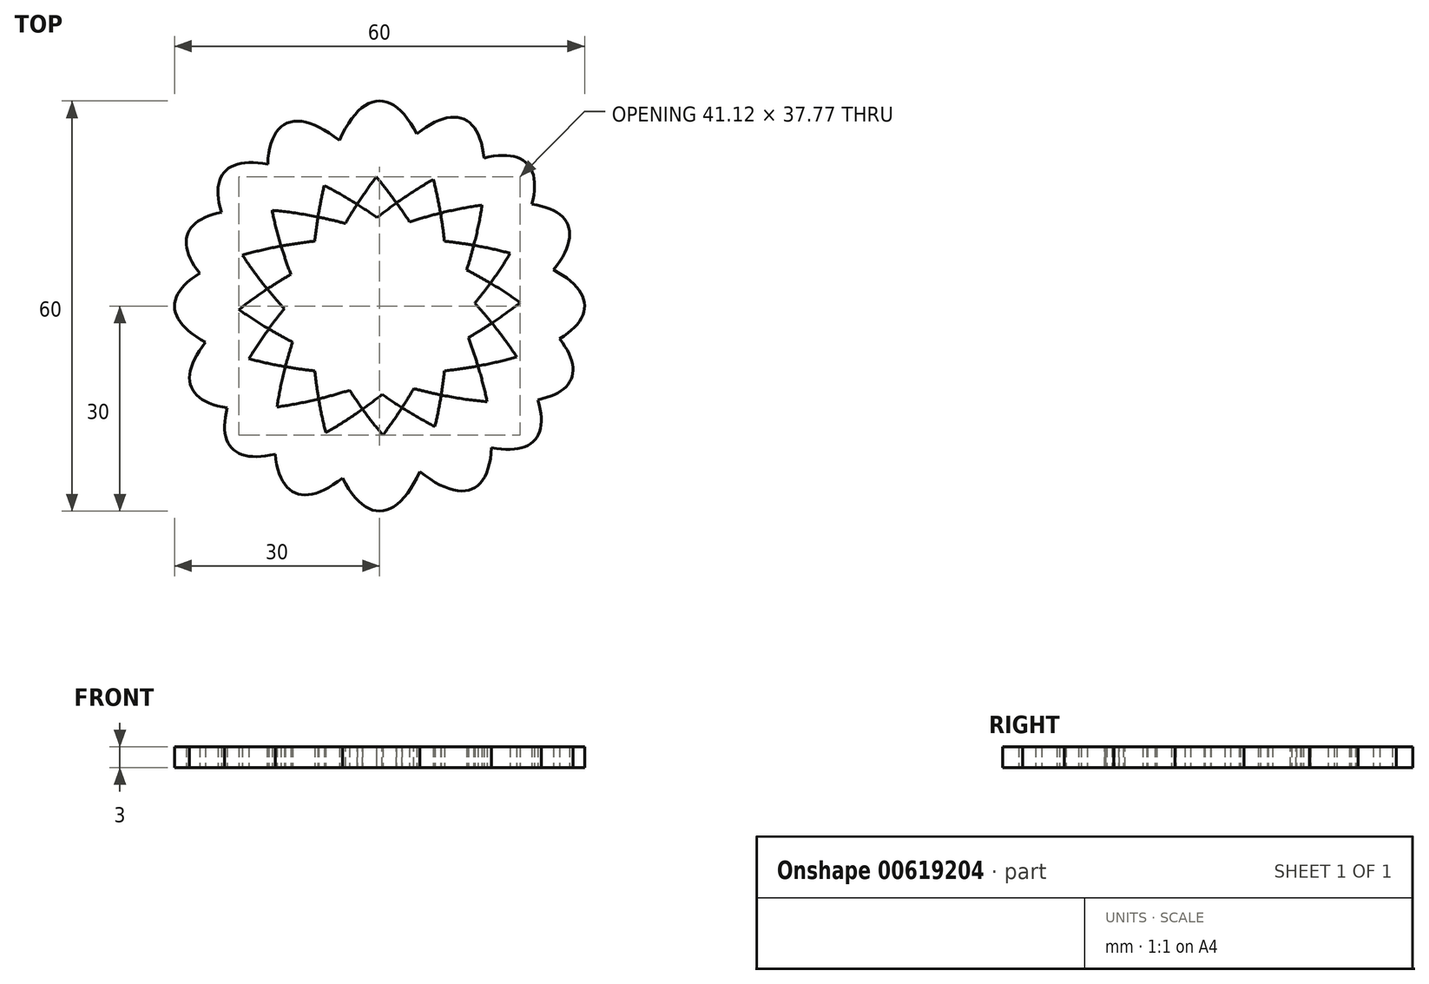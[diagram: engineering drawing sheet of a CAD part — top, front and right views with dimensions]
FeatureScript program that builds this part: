
annotation { "Feature Type Name" : "Feature", "Feature Type Description" : "" }
export const myFeature = defineFeature(function(context is Context, id is Id, definition is map)
    precondition{}
    {
        {
            var Q0;
            Q0=qCreatedBy(makeId("Top.planeOp"),FACE);
            var sketch = newSketch(context, id + "F0", { "sketchPlane" : qUnion([Q0])});
            skEllipticalArc(sketch, "E0", {});
            skEllipticalArc(sketch, "E1", {});
            skEllipticalArc(sketch, "E2", {});
            skEllipticalArc(sketch, "E3", {});
            skEllipticalArc(sketch, "E4", {});
            skEllipticalArc(sketch, "E5", {});
            skEllipticalArc(sketch, "E6", {});
            skEllipticalArc(sketch, "E7", {});
            skEllipticalArc(sketch, "E8.trimOffspring", {});
            skEllipticalArc(sketch, "E9.trimOffspring", {});
            skEllipticalArc(sketch, "E10.trimOffspring", {});
            skEllipticalArc(sketch, "E11.trimOffspring", {});
            skEllipticalArc(sketch, "E12.trimOffspring", {});
            skEllipticalArc(sketch, "E13.trimOffspring", {});
            skEllipticalArc(sketch, "E14.trimOffspring", {});
            skEllipticalArc(sketch, "E15.trimOffspring", {});
            skEllipticalArc(sketch, "E16.trimOffspring", {});
            skEllipticalArc(sketch, "E17.trimOffspring", {});
            skEllipticalArc(sketch, "E18.trimOffspring", {});
            skEllipticalArc(sketch, "E19.trimOffspring", {});
            skEllipticalArc(sketch, "E20.trimOffspring", {});
            skEllipticalArc(sketch, "E21.trimOffspring", {});
            skEllipticalArc(sketch, "E22.trimOffspring", {});
            skEllipticalArc(sketch, "E23.trimOffspring", {});
            skEllipticalArc(sketch, "E24.trimOffspring", {});
            skEllipticalArc(sketch, "E25.trimOffspring", {});
            skEllipticalArc(sketch, "E26.trimOffspring", {});
            skEllipticalArc(sketch, "E27.trimOffspring", {});
            skEllipticalArc(sketch, "E28.trimOffspring", {});
            skEllipticalArc(sketch, "E29.trimOffspring", {});
            skEllipticalArc(sketch, "E30.trimOffspring", {});
            skEllipticalArc(sketch, "E31.trimOffspring", {});
            skEllipticalArc(sketch, "E32", {});
            skEllipticalArc(sketch, "E33", {});
            skEllipticalArc(sketch, "E34", {});
            skEllipticalArc(sketch, "E35", {});
            skEllipticalArc(sketch, "E36", {});
            skEllipticalArc(sketch, "E37", {});
            skEllipticalArc(sketch, "E38", {});
            skEllipticalArc(sketch, "E39", {});
            skEllipticalArc(sketch, "E40", {});
            skEllipticalArc(sketch, "E41", {});
            skEllipticalArc(sketch, "E42", {});
            skEllipticalArc(sketch, "E43", {});
            skEllipticalArc(sketch, "E44", {});
            skEllipticalArc(sketch, "E45", {});
            skEllipticalArc(sketch, "E46", {});
            skEllipticalArc(sketch, "E47", {});
            const initialGuessF0  = {"E0": [0, 0, 0, -1, 0.03, 0.01, 5.707652658227705, 0], "E1": [0, 0, -1, 0, 0.03, 0.01, 2.642024951638131, 3.141592653589793], "E2": [0, 0, 0.719676517800556, 0.6943095201179845, 0.03, 0.01, 4.047013061400929, 5.402548984350965], "E3": [0, 0, -0.7581335094198967, 0.6520993650469777, 0.03, 0.01, 2.6137857632382424, 3.141592653589793], "E4": [0, 0, -0.45874326626276485, 0.8885688581413205, 0.03, 0.01, 2.511853225270534, 3.141592653589793], "E5": [0, 0, 0.41320832804158036, 0.9106365233379791, 0.03, 0.01, 4.109892639118385, 5.42593323517256], "E6": [0, 0, -0.9359348451973232, 0.35217320390038603, 0.03, 0.01, 2.653348630316495, 3.141592653589793], "E7": [0, 0, -0.9172268162763845, -0.3983653693576886, 0.03, 0.01, 2.584183450086654, 3.141592653589793], "E8.trimOffspring": [0, 0, 0, -1, 0.03, 0.01, 0.9425783349267141, 2.2361722457786577], "E9.trimOffspring": [0, 0, -0.45874326626276485, 0.8885688581413205, 0.03, 0.01, 3.998280747334294, 5.314885321650993], "E10.trimOffspring": [0, 0, -0.7581335094198967, 0.6520993650469777, 0.03, 0.01, 3.9802901965482214, 5.340606972252871], "E11.trimOffspring": [0, 0, -0.9359348451973232, 0.35217320390038603, 0.03, 0.01, 4.023758446463335, 5.426497213435084], "E12.trimOffspring": [0, 0, -1, 0, 0.03, 0.01, 4.022228976418415, 5.444487764221157], "E13.trimOffspring": [0, 0, 0.719676517800556, 0.6943095201179845, 0.03, 0.01, 5.78620703741481, 0], "E14.trimOffspring": [0, 0, -0.9172268162763845, -0.3983653693576886, 0.03, 0.01, 3.9988447255968187, 5.401019514306045], "E15.trimOffspring": [0, 0, 0.41320832804158036, 0.9106365233379791, 0.03, 0.01, 5.7629630431196155, 0], "E16.trimOffspring": [0, 0, 0.719676517800556, 0.6943095201179845, 0.03, 0.01, 0.9054204078111355, 2.260956330761171], "E17.trimOffspring": [0, 0, 0, -1, 0.03, 0.01, 2.566060004637914, 3.141592653589793], "E18.trimOffspring": [0, 0, 0.41320832804158036, 0.9106365233379791, 0.03, 0.01, 0.9682999855285929, 2.284340581582767], "E19.trimOffspring": [0, 0, -0.45874326626276485, 0.8885688581413205, 0.03, 0.01, 5.653445878860328, 0], "E20.trimOffspring": [0, 0, 0, -1, 0.03, 0.01, 4.084170988516508, 5.377764899368451], "E21.trimOffspring": [0, 0, -0.7581335094198967, 0.6520993650469777, 0.03, 0.01, 5.7553784168280355, 0], "E22.trimOffspring": [0, 0, -0.45874326626276485, 0.8885688581413205, 0.03, 0.01, 0.856688093744502, 2.1732926680612006], "E23.trimOffspring": [0, 0, -0.9359348451973232, 0.35217320390038603, 0.03, 0.01, 5.7949412839062875, 0], "E24.trimOffspring": [0, 0, -0.7581335094198967, 0.6520993650469777, 0.03, 0.01, 0.8386975429584291, 2.199014318663079], "E25.trimOffspring": [0, 0, -1, 0, 0.03, 0.01, 5.783617605227924, 0], "E26.trimOffspring": [0, 0, -0.9359348451973232, 0.35217320390038603, 0.03, 0.01, 0.8821657928735414, 2.284904559845293], "E27.trimOffspring": [0, 0, -0.9172268162763845, -0.3983653693576886, 0.03, 0.01, 5.725776103676448, 0], "E28.trimOffspring": [0, 0, -1, 0, 0.03, 0.01, 0.8806363228286226, 2.3028951106313644], "E29.trimOffspring": [0, 0, 0.719676517800556, 0.6943095201179845, 0.03, 0.01, 2.644614383825017, 3.141592653589793], "E30.trimOffspring": [0, 0, -0.9172268162763845, -0.3983653693576886, 0.03, 0.01, 0.857252072007026, 2.2594268607162515], "E31.trimOffspring": [0, 0, 0.41320832804158036, 0.9106365233379791, 0.03, 0.01, 2.6213703895298224, 3.141592653589793], "E32": [0, 0, -1, 0, 0.03, 0.01, 0, 0.5574092035031396], "E33": [0, 0, -0.9172268162763845, -0.3983653693576886, 0.03, 0.01, 0, 0.4969782697647762], "E34": [0, 0, 0.719676517800556, 0.6943095201179845, 0.03, 0.01, 3.141592653589793, 3.6618149176497643], "E35": [0, 0, 0.41320832804158036, 0.9106365233379791, 0.03, 0.01, 3.141592653589793, 3.7171253025416737], "E36": [0, 0, 0, -1, 0.03, 0.01, 0, 0.6297394283192591], "E37": [0, 0, -0.45874326626276485, 0.8885688581413205, 0.03, 0.01, 3.141592653589793, 3.6693995439413434], "E38": [0, 0, -0.7581335094198967, 0.6520993650469777, 0.03, 0.01, 3.141592653589793, 3.6298366768630923], "E39": [0, 0, -0.9359348451973232, 0.35217320390038603, 0.03, 0.01, 3.141592653589793, 3.6411603555414533], "E40": [0, 0, -1, 0, 0.03, 0.01, 3.141592653589793, 3.6990018570929326], "E41": [0, 0, -0.9172268162763845, -0.3983653693576886, 0.03, 0.01, 3.141592653589793, 3.6385709233545684], "E42": [0, 0, 0.719676517800556, 0.6943095201179845, 0.03, 0.01, 0, 0.5202222640599707], "E43": [0, 0, 0.41320832804158036, 0.9106365233379791, 0.03, 0.01, 0, 0.5755326489518812], "E44": [0, 0, 0, -1, 0.03, 0.01, 3.141592653589793, 3.7713320819090503], "E45": [0, 0, -0.45874326626276485, 0.8885688581413205, 0.03, 0.01, 0, 0.5278068903515505], "E46": [0, 0, -0.7581335094198967, 0.6520993650469777, 0.03, 0.01, 0, 0.48824402327329985], "E47": [0, 0, -0.9359348451973232, 0.35217320390038603, 0.03, 0.01, 0, 0.4995677019516617]};
            skSetInitialGuess(sketch, initialGuessF0);
            skSolve(sketch);
        }
        {
            var Q0;
            Q0=makeQuery(id+"F0.imprint","IMPRINT",FACE,{"disambiguationData":[TD([[makeQuery(id+"F0.imprint","IMPRINT",EDGE,{"derivedFrom":sQuery(id+"F0.wireOp",EDGE,"E0")}),1.0]])]});
            var Q1;
            {var subQ17=sQuery(id+"F0.wireOp",EDGE,"E2");var subQ21=sQuery(id+"F0.wireOp",EDGE,"E30.trimOffspring");var subQ22=makeQuery(id+"F0.imprint","INTERSECT",VERTEX,{"derivedFrom":[subQ17,subQ21]});Q1=makeQuery(id+"F0.imprint","IMPRINT",FACE,{"disambiguationData":[TD([[makeQuery(id+"F0.imprint","IMPRINT",EDGE,{"disambiguationData":[TD([[subQ22,-1.0]])],"derivedFrom":subQ17}),1.0]])]});}
            var Q2;
            {var subQ0=sQuery(id+"F0.wireOp",EDGE,"E14.trimOffspring");var subQ1=sQuery(id+"F0.wireOp",EDGE,"E9.trimOffspring");var subQ2=makeQuery(id+"F0.imprint","INTERSECT",VERTEX,{"derivedFrom":[subQ1,subQ0]});Q2=makeQuery(id+"F0.imprint","IMPRINT",FACE,{"disambiguationData":[TD([[makeQuery(id+"F0.imprint","IMPRINT",EDGE,{"disambiguationData":[TD([[subQ2,-1.0]])],"derivedFrom":subQ1}),1.0]])]});}
            var Q3;
            {var subQ0=sQuery(id+"F0.wireOp",EDGE,"E12.trimOffspring");var subQ1=sQuery(id+"F0.wireOp",EDGE,"E8.trimOffspring");var subQ2=makeQuery(id+"F0.imprint","INTERSECT",VERTEX,{"derivedFrom":[subQ1,subQ0]});Q3=makeQuery(id+"F0.imprint","IMPRINT",FACE,{"disambiguationData":[TD([[makeQuery(id+"F0.imprint","IMPRINT",EDGE,{"disambiguationData":[TD([[subQ2,-1.0]])],"derivedFrom":subQ1}),1.0]])]});}
            var Q4;
            {var subQ0=sQuery(id+"F0.wireOp",EDGE,"E11.trimOffspring");var subQ1=sQuery(id+"F0.wireOp",EDGE,"E8.trimOffspring");var subQ2=makeQuery(id+"F0.imprint","INTERSECT",VERTEX,{"derivedFrom":[subQ1,subQ0]});Q4=makeQuery(id+"F0.imprint","IMPRINT",FACE,{"disambiguationData":[TD([[makeQuery(id+"F0.imprint","IMPRINT",EDGE,{"disambiguationData":[TD([[subQ2,-1.0]])],"derivedFrom":subQ1}),1.0]])]});}
            var Q5;
            {var subQ0=sQuery(id+"F0.wireOp",EDGE,"E11.trimOffspring");var subQ1=sQuery(id+"F0.wireOp",EDGE,"E5");var subQ2=makeQuery(id+"F0.imprint","INTERSECT",VERTEX,{"derivedFrom":[subQ1,subQ0]});Q5=makeQuery(id+"F0.imprint","IMPRINT",FACE,{"disambiguationData":[TD([[makeQuery(id+"F0.imprint","IMPRINT",EDGE,{"disambiguationData":[TD([[subQ2,-1.0]])],"derivedFrom":subQ1}),1.0]])]});}
            var Q6;
            {var subQ0=sQuery(id+"F0.wireOp",EDGE,"E10.trimOffspring");var subQ1=sQuery(id+"F0.wireOp",EDGE,"E5");var subQ2=makeQuery(id+"F0.imprint","INTERSECT",VERTEX,{"derivedFrom":[subQ1,subQ0]});Q6=makeQuery(id+"F0.imprint","IMPRINT",FACE,{"disambiguationData":[TD([[makeQuery(id+"F0.imprint","IMPRINT",EDGE,{"disambiguationData":[TD([[subQ2,-1.0]])],"derivedFrom":subQ1}),1.0]])]});}
            var Q7;
            {var subQ0=sQuery(id+"F0.wireOp",EDGE,"E10.trimOffspring");var subQ1=sQuery(id+"F0.wireOp",EDGE,"E2");var subQ2=makeQuery(id+"F0.imprint","INTERSECT",VERTEX,{"derivedFrom":[subQ1,subQ0]});Q7=makeQuery(id+"F0.imprint","IMPRINT",FACE,{"disambiguationData":[TD([[makeQuery(id+"F0.imprint","IMPRINT",EDGE,{"disambiguationData":[TD([[subQ2,-1.0]])],"derivedFrom":subQ1}),1.0]])]});}
            var Q8;
            {var subQ0=sQuery(id+"F0.wireOp",EDGE,"E10.trimOffspring");var subQ1=sQuery(id+"F0.wireOp",EDGE,"E8.trimOffspring");var subQ2=makeQuery(id+"F0.imprint","INTERSECT",VERTEX,{"derivedFrom":[subQ1,subQ0]});Q8=makeQuery(id+"F0.imprint","IMPRINT",FACE,{"disambiguationData":[TD([[makeQuery(id+"F0.imprint","IMPRINT",EDGE,{"disambiguationData":[TD([[subQ2,-1.0]])],"derivedFrom":subQ1}),1.0]])]});}
            var Q9;
            {var subQ0=sQuery(id+"F0.wireOp",EDGE,"E9.trimOffspring");var subQ1=sQuery(id+"F0.wireOp",EDGE,"E2");var subQ2=makeQuery(id+"F0.imprint","INTERSECT",VERTEX,{"derivedFrom":[subQ1,subQ0]});Q9=makeQuery(id+"F0.imprint","IMPRINT",FACE,{"disambiguationData":[TD([[makeQuery(id+"F0.imprint","IMPRINT",EDGE,{"disambiguationData":[TD([[subQ2,-1.0]])],"derivedFrom":subQ1}),1.0]])]});}
            var Q10;
            {var subQ0=sQuery(id+"F0.wireOp",EDGE,"E9.trimOffspring");var subQ1=sQuery(id+"F0.wireOp",EDGE,"E2");var subQ2=makeQuery(id+"F0.imprint","INTERSECT",VERTEX,{"derivedFrom":[subQ1,subQ0]});Q10=makeQuery(id+"F0.imprint","IMPRINT",FACE,{"disambiguationData":[TD([[makeQuery(id+"F0.imprint","IMPRINT",EDGE,{"disambiguationData":[TD([[subQ2,-1.0]])],"derivedFrom":subQ1}),-1.0]])]});}
            var Q11;
            {var subQ0=sQuery(id+"F0.wireOp",EDGE,"E28.trimOffspring");var subQ1=sQuery(id+"F0.wireOp",EDGE,"E8.trimOffspring");var subQ2=makeQuery(id+"F0.imprint","INTERSECT",VERTEX,{"derivedFrom":[subQ1,subQ0]});Q11=makeQuery(id+"F0.imprint","IMPRINT",FACE,{"disambiguationData":[TD([[makeQuery(id+"F0.imprint","IMPRINT",EDGE,{"disambiguationData":[TD([[subQ2,-1.0]])],"derivedFrom":subQ1}),-1.0]])]});}
            var Q12;
            {var subQ0=sQuery(id+"F0.wireOp",EDGE,"E8.trimOffspring");var subQ1=sQuery(id+"F0.wireOp",EDGE,"E2");var subQ2=makeQuery(id+"F0.imprint","INTERSECT",VERTEX,{"derivedFrom":[subQ1,subQ0]});Q12=makeQuery(id+"F0.imprint","IMPRINT",FACE,{"disambiguationData":[TD([[makeQuery(id+"F0.imprint","IMPRINT",EDGE,{"disambiguationData":[TD([[subQ2,-1.0]])],"derivedFrom":subQ1}),1.0]])]});}
            var Q13;
            {var subQ0=sQuery(id+"F0.wireOp",EDGE,"E8.trimOffspring");var subQ1=sQuery(id+"F0.wireOp",EDGE,"E2");var subQ2=makeQuery(id+"F0.imprint","INTERSECT",VERTEX,{"derivedFrom":[subQ1,subQ0]});Q13=makeQuery(id+"F0.imprint","IMPRINT",FACE,{"disambiguationData":[TD([[makeQuery(id+"F0.imprint","IMPRINT",EDGE,{"disambiguationData":[TD([[subQ2,-1.0]])],"derivedFrom":subQ1}),-1.0]])]});}
            var Q14;
            {var subQ0=sQuery(id+"F0.wireOp",EDGE,"E5");var subQ1=sQuery(id+"F0.wireOp",EDGE,"E2");var subQ2=makeQuery(id+"F0.imprint","INTERSECT",VERTEX,{"derivedFrom":[subQ1,subQ0]});Q14=makeQuery(id+"F0.imprint","IMPRINT",FACE,{"disambiguationData":[TD([[makeQuery(id+"F0.imprint","IMPRINT",EDGE,{"disambiguationData":[TD([[subQ2,-1.0]])],"derivedFrom":subQ1}),-1.0]])]});}
            var Q15;
            {var subQ0=sQuery(id+"F0.wireOp",EDGE,"E28.trimOffspring");var subQ1=sQuery(id+"F0.wireOp",EDGE,"E5");var subQ2=makeQuery(id+"F0.imprint","INTERSECT",VERTEX,{"derivedFrom":[subQ1,subQ0]});Q15=makeQuery(id+"F0.imprint","IMPRINT",FACE,{"disambiguationData":[TD([[makeQuery(id+"F0.imprint","IMPRINT",EDGE,{"disambiguationData":[TD([[subQ2,-1.0]])],"derivedFrom":subQ1}),-1.0]])]});}
            var Q16;
            {var subQ0=sQuery(id+"F0.wireOp",EDGE,"E26.trimOffspring");var subQ1=sQuery(id+"F0.wireOp",EDGE,"E5");var subQ2=makeQuery(id+"F0.imprint","INTERSECT",VERTEX,{"derivedFrom":[subQ1,subQ0]});Q16=makeQuery(id+"F0.imprint","IMPRINT",FACE,{"disambiguationData":[TD([[makeQuery(id+"F0.imprint","IMPRINT",EDGE,{"disambiguationData":[TD([[subQ2,-1.0]])],"derivedFrom":subQ1}),-1.0]])]});}
            var Q17;
            {var subQ0=sQuery(id+"F0.wireOp",EDGE,"E24.trimOffspring");var subQ1=sQuery(id+"F0.wireOp",EDGE,"E2");var subQ2=makeQuery(id+"F0.imprint","INTERSECT",VERTEX,{"derivedFrom":[subQ1,subQ0]});Q17=makeQuery(id+"F0.imprint","IMPRINT",FACE,{"disambiguationData":[TD([[makeQuery(id+"F0.imprint","IMPRINT",EDGE,{"disambiguationData":[TD([[subQ2,-1.0]])],"derivedFrom":subQ1}),-1.0]])]});}
            var Q18;
            {var subQ0=sQuery(id+"F0.wireOp",EDGE,"E26.trimOffspring");var subQ1=sQuery(id+"F0.wireOp",EDGE,"E2");var subQ2=makeQuery(id+"F0.imprint","INTERSECT",VERTEX,{"derivedFrom":[subQ1,subQ0]});Q18=makeQuery(id+"F0.imprint","IMPRINT",FACE,{"disambiguationData":[TD([[makeQuery(id+"F0.imprint","IMPRINT",EDGE,{"disambiguationData":[TD([[subQ2,-1.0]])],"derivedFrom":subQ1}),-1.0]])]});}
            var Q19;
            {var subQ0=sQuery(id+"F0.wireOp",EDGE,"E9.trimOffspring");var subQ1=sQuery(id+"F0.wireOp",EDGE,"E5");var subQ2=makeQuery(id+"F0.imprint","INTERSECT",VERTEX,{"derivedFrom":[subQ1,subQ0]});Q19=makeQuery(id+"F0.imprint","IMPRINT",FACE,{"disambiguationData":[TD([[makeQuery(id+"F0.imprint","IMPRINT",EDGE,{"disambiguationData":[TD([[subQ2,-1.0]])],"derivedFrom":subQ1}),1.0]])]});}
            var Q20;
            {var subQ0=sQuery(id+"F0.wireOp",EDGE,"E28.trimOffspring");var subQ1=sQuery(id+"F0.wireOp",EDGE,"E2");var subQ2=makeQuery(id+"F0.imprint","INTERSECT",VERTEX,{"derivedFrom":[subQ1,subQ0]});Q20=makeQuery(id+"F0.imprint","IMPRINT",FACE,{"disambiguationData":[TD([[makeQuery(id+"F0.imprint","IMPRINT",EDGE,{"disambiguationData":[TD([[subQ2,-1.0]])],"derivedFrom":subQ1}),-1.0]])]});}
            var Q21;
            {var subQ0=sQuery(id+"F0.wireOp",EDGE,"E30.trimOffspring");var subQ1=sQuery(id+"F0.wireOp",EDGE,"E2");var subQ2=makeQuery(id+"F0.imprint","INTERSECT",VERTEX,{"derivedFrom":[subQ1,subQ0]});Q21=makeQuery(id+"F0.imprint","IMPRINT",FACE,{"disambiguationData":[TD([[makeQuery(id+"F0.imprint","IMPRINT",EDGE,{"disambiguationData":[TD([[subQ2,-1.0]])],"derivedFrom":subQ1}),-1.0]])]});}
            var Q22;
            {var subQ0=sQuery(id+"F0.wireOp",EDGE,"E5");var subQ1=sQuery(id+"F0.wireOp",EDGE,"E2");var subQ2=makeQuery(id+"F0.imprint","INTERSECT",VERTEX,{"derivedFrom":[subQ1,subQ0]});Q22=makeQuery(id+"F0.imprint","IMPRINT",FACE,{"disambiguationData":[TD([[makeQuery(id+"F0.imprint","IMPRINT",EDGE,{"disambiguationData":[TD([[subQ2,-1.0]])],"derivedFrom":subQ1}),1.0]])]});}
            var Q23;
            {var subQ0=sQuery(id+"F0.wireOp",EDGE,"E8.trimOffspring");var subQ1=sQuery(id+"F0.wireOp",EDGE,"E5");var subQ2=makeQuery(id+"F0.imprint","INTERSECT",VERTEX,{"derivedFrom":[subQ1,subQ0]});Q23=makeQuery(id+"F0.imprint","IMPRINT",FACE,{"disambiguationData":[TD([[makeQuery(id+"F0.imprint","IMPRINT",EDGE,{"disambiguationData":[TD([[subQ2,-1.0]])],"derivedFrom":subQ1}),1.0]])]});}
            var Q24;
            {var subQ0=sQuery(id+"F0.wireOp",EDGE,"E9.trimOffspring");var subQ1=sQuery(id+"F0.wireOp",EDGE,"E8.trimOffspring");var subQ2=makeQuery(id+"F0.imprint","INTERSECT",VERTEX,{"derivedFrom":[subQ1,subQ0]});Q24=makeQuery(id+"F0.imprint","IMPRINT",FACE,{"disambiguationData":[TD([[makeQuery(id+"F0.imprint","IMPRINT",EDGE,{"disambiguationData":[TD([[subQ2,-1.0]])],"derivedFrom":subQ1}),1.0]])]});}
            var Q25;
            {var subQ0=sQuery(id+"F0.wireOp",EDGE,"E10.trimOffspring");var subQ1=sQuery(id+"F0.wireOp",EDGE,"E9.trimOffspring");var subQ2=makeQuery(id+"F0.imprint","INTERSECT",VERTEX,{"derivedFrom":[subQ1,subQ0]});Q25=makeQuery(id+"F0.imprint","IMPRINT",FACE,{"disambiguationData":[TD([[makeQuery(id+"F0.imprint","IMPRINT",EDGE,{"disambiguationData":[TD([[subQ2,-1.0]])],"derivedFrom":subQ1}),1.0]])]});}
            var Q26;
            {var subQ0=sQuery(id+"F0.wireOp",EDGE,"E11.trimOffspring");var subQ1=sQuery(id+"F0.wireOp",EDGE,"E9.trimOffspring");var subQ2=makeQuery(id+"F0.imprint","INTERSECT",VERTEX,{"derivedFrom":[subQ1,subQ0]});Q26=makeQuery(id+"F0.imprint","IMPRINT",FACE,{"disambiguationData":[TD([[makeQuery(id+"F0.imprint","IMPRINT",EDGE,{"disambiguationData":[TD([[subQ2,-1.0]])],"derivedFrom":subQ1}),1.0]])]});}
            var Q27;
            {var subQ0=sQuery(id+"F0.wireOp",EDGE,"E12.trimOffspring");var subQ1=sQuery(id+"F0.wireOp",EDGE,"E9.trimOffspring");var subQ2=makeQuery(id+"F0.imprint","INTERSECT",VERTEX,{"derivedFrom":[subQ1,subQ0]});Q27=makeQuery(id+"F0.imprint","IMPRINT",FACE,{"disambiguationData":[TD([[makeQuery(id+"F0.imprint","IMPRINT",EDGE,{"disambiguationData":[TD([[subQ2,-1.0]])],"derivedFrom":subQ1}),1.0]])]});}
            var Q28;
            {var subQ0=sQuery(id+"F0.wireOp",EDGE,"E12.trimOffspring");var subQ1=sQuery(id+"F0.wireOp",EDGE,"E10.trimOffspring");var subQ2=makeQuery(id+"F0.imprint","INTERSECT",VERTEX,{"derivedFrom":[subQ1,subQ0]});Q28=makeQuery(id+"F0.imprint","IMPRINT",FACE,{"disambiguationData":[TD([[makeQuery(id+"F0.imprint","IMPRINT",EDGE,{"disambiguationData":[TD([[subQ2,-1.0]])],"derivedFrom":subQ1}),1.0]])]});}
            var Q29;
            {var subQ0=sQuery(id+"F0.wireOp",EDGE,"E11.trimOffspring");var subQ1=sQuery(id+"F0.wireOp",EDGE,"E10.trimOffspring");var subQ2=makeQuery(id+"F0.imprint","INTERSECT",VERTEX,{"derivedFrom":[subQ1,subQ0]});Q29=makeQuery(id+"F0.imprint","IMPRINT",FACE,{"disambiguationData":[TD([[makeQuery(id+"F0.imprint","IMPRINT",EDGE,{"disambiguationData":[TD([[subQ2,-1.0]])],"derivedFrom":subQ1}),1.0]])]});}
            var Q30;
            {var subQ0=sQuery(id+"F0.wireOp",EDGE,"E12.trimOffspring");var subQ1=sQuery(id+"F0.wireOp",EDGE,"E11.trimOffspring");var subQ2=makeQuery(id+"F0.imprint","INTERSECT",VERTEX,{"derivedFrom":[subQ1,subQ0]});Q30=makeQuery(id+"F0.imprint","IMPRINT",FACE,{"disambiguationData":[TD([[makeQuery(id+"F0.imprint","IMPRINT",EDGE,{"disambiguationData":[TD([[subQ2,-1.0]])],"derivedFrom":subQ1}),1.0]])]});}
            var Q31;
            {var subQ0=sQuery(id+"F0.wireOp",EDGE,"E14.trimOffspring");var subQ1=sQuery(id+"F0.wireOp",EDGE,"E11.trimOffspring");var subQ2=makeQuery(id+"F0.imprint","INTERSECT",VERTEX,{"derivedFrom":[subQ1,subQ0]});Q31=makeQuery(id+"F0.imprint","IMPRINT",FACE,{"disambiguationData":[TD([[makeQuery(id+"F0.imprint","IMPRINT",EDGE,{"disambiguationData":[TD([[subQ2,-1.0]])],"derivedFrom":subQ1}),1.0]])]});}
            var Q32;
            {var subQ0=sQuery(id+"F0.wireOp",EDGE,"E14.trimOffspring");var subQ1=sQuery(id+"F0.wireOp",EDGE,"E10.trimOffspring");var subQ2=makeQuery(id+"F0.imprint","INTERSECT",VERTEX,{"derivedFrom":[subQ1,subQ0]});Q32=makeQuery(id+"F0.imprint","IMPRINT",FACE,{"disambiguationData":[TD([[makeQuery(id+"F0.imprint","IMPRINT",EDGE,{"disambiguationData":[TD([[subQ2,-1.0]])],"derivedFrom":subQ1}),1.0]])]});}
            var Q33;
            {var subQ0=sQuery(id+"F0.wireOp",EDGE,"E14.trimOffspring");var subQ1=sQuery(id+"F0.wireOp",EDGE,"E12.trimOffspring");var subQ2=makeQuery(id+"F0.imprint","INTERSECT",VERTEX,{"derivedFrom":[subQ1,subQ0]});Q33=makeQuery(id+"F0.imprint","IMPRINT",FACE,{"disambiguationData":[TD([[makeQuery(id+"F0.imprint","IMPRINT",EDGE,{"disambiguationData":[TD([[subQ2,-1.0]])],"derivedFrom":subQ1}),1.0]])]});}
            var Q34;
            {var subQ0=sQuery(id+"F0.wireOp",EDGE,"E16.trimOffspring");var subQ1=sQuery(id+"F0.wireOp",EDGE,"E12.trimOffspring");var subQ2=makeQuery(id+"F0.imprint","INTERSECT",VERTEX,{"derivedFrom":[subQ1,subQ0]});Q34=makeQuery(id+"F0.imprint","IMPRINT",FACE,{"disambiguationData":[TD([[makeQuery(id+"F0.imprint","IMPRINT",EDGE,{"disambiguationData":[TD([[subQ2,-1.0]])],"derivedFrom":subQ1}),1.0]])]});}
            var Q35;
            {var subQ0=sQuery(id+"F0.wireOp",EDGE,"E16.trimOffspring");var subQ1=sQuery(id+"F0.wireOp",EDGE,"E11.trimOffspring");var subQ2=makeQuery(id+"F0.imprint","INTERSECT",VERTEX,{"derivedFrom":[subQ1,subQ0]});Q35=makeQuery(id+"F0.imprint","IMPRINT",FACE,{"disambiguationData":[TD([[makeQuery(id+"F0.imprint","IMPRINT",EDGE,{"disambiguationData":[TD([[subQ2,-1.0]])],"derivedFrom":subQ1}),1.0]])]});}
            var Q36;
            {var subQ0=sQuery(id+"F0.wireOp",EDGE,"E16.trimOffspring");var subQ1=sQuery(id+"F0.wireOp",EDGE,"E10.trimOffspring");var subQ2=makeQuery(id+"F0.imprint","INTERSECT",VERTEX,{"derivedFrom":[subQ1,subQ0]});Q36=makeQuery(id+"F0.imprint","IMPRINT",FACE,{"disambiguationData":[TD([[makeQuery(id+"F0.imprint","IMPRINT",EDGE,{"disambiguationData":[TD([[subQ2,-1.0]])],"derivedFrom":subQ1}),1.0]])]});}
            var Q37;
            {var subQ0=sQuery(id+"F0.wireOp",EDGE,"E16.trimOffspring");var subQ1=sQuery(id+"F0.wireOp",EDGE,"E14.trimOffspring");var subQ2=makeQuery(id+"F0.imprint","INTERSECT",VERTEX,{"derivedFrom":[subQ1,subQ0]});Q37=makeQuery(id+"F0.imprint","IMPRINT",FACE,{"disambiguationData":[TD([[makeQuery(id+"F0.imprint","IMPRINT",EDGE,{"disambiguationData":[TD([[subQ2,-1.0]])],"derivedFrom":subQ1}),1.0]])]});}
            var Q38;
            {var subQ0=sQuery(id+"F0.wireOp",EDGE,"E18.trimOffspring");var subQ1=sQuery(id+"F0.wireOp",EDGE,"E14.trimOffspring");var subQ2=makeQuery(id+"F0.imprint","INTERSECT",VERTEX,{"derivedFrom":[subQ1,subQ0]});Q38=makeQuery(id+"F0.imprint","IMPRINT",FACE,{"disambiguationData":[TD([[makeQuery(id+"F0.imprint","IMPRINT",EDGE,{"disambiguationData":[TD([[subQ2,-1.0]])],"derivedFrom":subQ1}),1.0]])]});}
            var Q39;
            {var subQ0=sQuery(id+"F0.wireOp",EDGE,"E18.trimOffspring");var subQ1=sQuery(id+"F0.wireOp",EDGE,"E16.trimOffspring");var subQ2=makeQuery(id+"F0.imprint","INTERSECT",VERTEX,{"derivedFrom":[subQ1,subQ0]});Q39=makeQuery(id+"F0.imprint","IMPRINT",FACE,{"disambiguationData":[TD([[makeQuery(id+"F0.imprint","IMPRINT",EDGE,{"disambiguationData":[TD([[subQ2,-1.0]])],"derivedFrom":subQ1}),1.0]])]});}
            var Q40;
            {var subQ0=sQuery(id+"F0.wireOp",EDGE,"E18.trimOffspring");var subQ1=sQuery(id+"F0.wireOp",EDGE,"E12.trimOffspring");var subQ2=makeQuery(id+"F0.imprint","INTERSECT",VERTEX,{"derivedFrom":[subQ1,subQ0]});Q40=makeQuery(id+"F0.imprint","IMPRINT",FACE,{"disambiguationData":[TD([[makeQuery(id+"F0.imprint","IMPRINT",EDGE,{"disambiguationData":[TD([[subQ2,-1.0]])],"derivedFrom":subQ1}),1.0]])]});}
            var Q41;
            {var subQ0=sQuery(id+"F0.wireOp",EDGE,"E18.trimOffspring");var subQ1=sQuery(id+"F0.wireOp",EDGE,"E11.trimOffspring");var subQ2=makeQuery(id+"F0.imprint","INTERSECT",VERTEX,{"derivedFrom":[subQ1,subQ0]});Q41=makeQuery(id+"F0.imprint","IMPRINT",FACE,{"disambiguationData":[TD([[makeQuery(id+"F0.imprint","IMPRINT",EDGE,{"disambiguationData":[TD([[subQ2,-1.0]])],"derivedFrom":subQ1}),1.0]])]});}
            var Q42;
            {var subQ0=sQuery(id+"F0.wireOp",EDGE,"E20.trimOffspring");var subQ1=sQuery(id+"F0.wireOp",EDGE,"E12.trimOffspring");var subQ2=makeQuery(id+"F0.imprint","INTERSECT",VERTEX,{"derivedFrom":[subQ1,subQ0]});Q42=makeQuery(id+"F0.imprint","IMPRINT",FACE,{"disambiguationData":[TD([[makeQuery(id+"F0.imprint","IMPRINT",EDGE,{"disambiguationData":[TD([[subQ2,-1.0]])],"derivedFrom":subQ1}),1.0]])]});}
            var Q43;
            {var subQ0=sQuery(id+"F0.wireOp",EDGE,"E22.trimOffspring");var subQ1=sQuery(id+"F0.wireOp",EDGE,"E14.trimOffspring");var subQ2=makeQuery(id+"F0.imprint","INTERSECT",VERTEX,{"derivedFrom":[subQ1,subQ0]});Q43=makeQuery(id+"F0.imprint","IMPRINT",FACE,{"disambiguationData":[TD([[makeQuery(id+"F0.imprint","IMPRINT",EDGE,{"disambiguationData":[TD([[subQ2,-1.0]])],"derivedFrom":subQ1}),1.0]])]});}
            var Q44;
            {var subQ0=sQuery(id+"F0.wireOp",EDGE,"E20.trimOffspring");var subQ1=sQuery(id+"F0.wireOp",EDGE,"E14.trimOffspring");var subQ2=makeQuery(id+"F0.imprint","INTERSECT",VERTEX,{"derivedFrom":[subQ1,subQ0]});Q44=makeQuery(id+"F0.imprint","IMPRINT",FACE,{"disambiguationData":[TD([[makeQuery(id+"F0.imprint","IMPRINT",EDGE,{"disambiguationData":[TD([[subQ2,-1.0]])],"derivedFrom":subQ1}),1.0]])]});}
            var Q45;
            {var subQ0=sQuery(id+"F0.wireOp",EDGE,"E20.trimOffspring");var subQ1=sQuery(id+"F0.wireOp",EDGE,"E16.trimOffspring");var subQ2=makeQuery(id+"F0.imprint","INTERSECT",VERTEX,{"derivedFrom":[subQ1,subQ0]});Q45=makeQuery(id+"F0.imprint","IMPRINT",FACE,{"disambiguationData":[TD([[makeQuery(id+"F0.imprint","IMPRINT",EDGE,{"disambiguationData":[TD([[subQ2,-1.0]])],"derivedFrom":subQ1}),1.0]])]});}
            var Q46;
            {var subQ0=sQuery(id+"F0.wireOp",EDGE,"E20.trimOffspring");var subQ1=sQuery(id+"F0.wireOp",EDGE,"E18.trimOffspring");var subQ2=makeQuery(id+"F0.imprint","INTERSECT",VERTEX,{"derivedFrom":[subQ1,subQ0]});Q46=makeQuery(id+"F0.imprint","IMPRINT",FACE,{"disambiguationData":[TD([[makeQuery(id+"F0.imprint","IMPRINT",EDGE,{"disambiguationData":[TD([[subQ2,-1.0]])],"derivedFrom":subQ1}),1.0]])]});}
            var Q47;
            {var subQ0=sQuery(id+"F0.wireOp",EDGE,"E22.trimOffspring");var subQ1=sQuery(id+"F0.wireOp",EDGE,"E16.trimOffspring");var subQ2=makeQuery(id+"F0.imprint","INTERSECT",VERTEX,{"derivedFrom":[subQ1,subQ0]});Q47=makeQuery(id+"F0.imprint","IMPRINT",FACE,{"disambiguationData":[TD([[makeQuery(id+"F0.imprint","IMPRINT",EDGE,{"disambiguationData":[TD([[subQ2,-1.0]])],"derivedFrom":subQ1}),1.0]])]});}
            var Q48;
            {var subQ0=sQuery(id+"F0.wireOp",EDGE,"E22.trimOffspring");var subQ1=sQuery(id+"F0.wireOp",EDGE,"E18.trimOffspring");var subQ2=makeQuery(id+"F0.imprint","INTERSECT",VERTEX,{"derivedFrom":[subQ1,subQ0]});Q48=makeQuery(id+"F0.imprint","IMPRINT",FACE,{"disambiguationData":[TD([[makeQuery(id+"F0.imprint","IMPRINT",EDGE,{"disambiguationData":[TD([[subQ2,-1.0]])],"derivedFrom":subQ1}),1.0]])]});}
            var Q49;
            {var subQ0=sQuery(id+"F0.wireOp",EDGE,"E24.trimOffspring");var subQ1=sQuery(id+"F0.wireOp",EDGE,"E16.trimOffspring");var subQ2=makeQuery(id+"F0.imprint","INTERSECT",VERTEX,{"derivedFrom":[subQ1,subQ0]});Q49=makeQuery(id+"F0.imprint","IMPRINT",FACE,{"disambiguationData":[TD([[makeQuery(id+"F0.imprint","IMPRINT",EDGE,{"disambiguationData":[TD([[subQ2,-1.0]])],"derivedFrom":subQ1}),1.0]])]});}
            var Q50;
            {var subQ0=sQuery(id+"F0.wireOp",EDGE,"E24.trimOffspring");var subQ1=sQuery(id+"F0.wireOp",EDGE,"E18.trimOffspring");var subQ2=makeQuery(id+"F0.imprint","INTERSECT",VERTEX,{"derivedFrom":[subQ1,subQ0]});Q50=makeQuery(id+"F0.imprint","IMPRINT",FACE,{"disambiguationData":[TD([[makeQuery(id+"F0.imprint","IMPRINT",EDGE,{"disambiguationData":[TD([[subQ2,-1.0]])],"derivedFrom":subQ1}),1.0]])]});}
            var Q51;
            {var subQ0=sQuery(id+"F0.wireOp",EDGE,"E26.trimOffspring");var subQ1=sQuery(id+"F0.wireOp",EDGE,"E18.trimOffspring");var subQ2=makeQuery(id+"F0.imprint","INTERSECT",VERTEX,{"derivedFrom":[subQ1,subQ0]});Q51=makeQuery(id+"F0.imprint","IMPRINT",FACE,{"disambiguationData":[TD([[makeQuery(id+"F0.imprint","IMPRINT",EDGE,{"disambiguationData":[TD([[subQ2,-1.0]])],"derivedFrom":subQ1}),1.0]])]});}
            var Q52;
            {var subQ0=sQuery(id+"F0.wireOp",EDGE,"E24.trimOffspring");var subQ1=sQuery(id+"F0.wireOp",EDGE,"E20.trimOffspring");var subQ2=makeQuery(id+"F0.imprint","INTERSECT",VERTEX,{"derivedFrom":[subQ1,subQ0]});Q52=makeQuery(id+"F0.imprint","IMPRINT",FACE,{"disambiguationData":[TD([[makeQuery(id+"F0.imprint","IMPRINT",EDGE,{"disambiguationData":[TD([[subQ2,-1.0]])],"derivedFrom":subQ1}),1.0]])]});}
            var Q53;
            {var subQ0=sQuery(id+"F0.wireOp",EDGE,"E22.trimOffspring");var subQ1=sQuery(id+"F0.wireOp",EDGE,"E20.trimOffspring");var subQ2=makeQuery(id+"F0.imprint","INTERSECT",VERTEX,{"derivedFrom":[subQ1,subQ0]});Q53=makeQuery(id+"F0.imprint","IMPRINT",FACE,{"disambiguationData":[TD([[makeQuery(id+"F0.imprint","IMPRINT",EDGE,{"disambiguationData":[TD([[subQ2,-1.0]])],"derivedFrom":subQ1}),1.0]])]});}
            var Q54;
            {var subQ0=sQuery(id+"F0.wireOp",EDGE,"E26.trimOffspring");var subQ1=sQuery(id+"F0.wireOp",EDGE,"E20.trimOffspring");var subQ2=makeQuery(id+"F0.imprint","INTERSECT",VERTEX,{"derivedFrom":[subQ1,subQ0]});Q54=makeQuery(id+"F0.imprint","IMPRINT",FACE,{"disambiguationData":[TD([[makeQuery(id+"F0.imprint","IMPRINT",EDGE,{"disambiguationData":[TD([[subQ2,-1.0]])],"derivedFrom":subQ1}),1.0]])]});}
            var Q55;
            {var subQ0=sQuery(id+"F0.wireOp",EDGE,"E24.trimOffspring");var subQ1=sQuery(id+"F0.wireOp",EDGE,"E22.trimOffspring");var subQ2=makeQuery(id+"F0.imprint","INTERSECT",VERTEX,{"derivedFrom":[subQ1,subQ0]});Q55=makeQuery(id+"F0.imprint","IMPRINT",FACE,{"disambiguationData":[TD([[makeQuery(id+"F0.imprint","IMPRINT",EDGE,{"disambiguationData":[TD([[subQ2,-1.0]])],"derivedFrom":subQ1}),1.0]])]});}
            var Q56;
            {var subQ0=sQuery(id+"F0.wireOp",EDGE,"E26.trimOffspring");var subQ1=sQuery(id+"F0.wireOp",EDGE,"E22.trimOffspring");var subQ2=makeQuery(id+"F0.imprint","INTERSECT",VERTEX,{"derivedFrom":[subQ1,subQ0]});Q56=makeQuery(id+"F0.imprint","IMPRINT",FACE,{"disambiguationData":[TD([[makeQuery(id+"F0.imprint","IMPRINT",EDGE,{"disambiguationData":[TD([[subQ2,-1.0]])],"derivedFrom":subQ1}),1.0]])]});}
            var Q57;
            {var subQ0=sQuery(id+"F0.wireOp",EDGE,"E28.trimOffspring");var subQ1=sQuery(id+"F0.wireOp",EDGE,"E20.trimOffspring");var subQ2=makeQuery(id+"F0.imprint","INTERSECT",VERTEX,{"derivedFrom":[subQ1,subQ0]});Q57=makeQuery(id+"F0.imprint","IMPRINT",FACE,{"disambiguationData":[TD([[makeQuery(id+"F0.imprint","IMPRINT",EDGE,{"disambiguationData":[TD([[subQ2,-1.0]])],"derivedFrom":subQ1}),1.0]])]});}
            var Q58;
            {var subQ0=sQuery(id+"F0.wireOp",EDGE,"E28.trimOffspring");var subQ1=sQuery(id+"F0.wireOp",EDGE,"E22.trimOffspring");var subQ2=makeQuery(id+"F0.imprint","INTERSECT",VERTEX,{"derivedFrom":[subQ1,subQ0]});Q58=makeQuery(id+"F0.imprint","IMPRINT",FACE,{"disambiguationData":[TD([[makeQuery(id+"F0.imprint","IMPRINT",EDGE,{"disambiguationData":[TD([[subQ2,-1.0]])],"derivedFrom":subQ1}),1.0]])]});}
            var Q59;
            {var subQ0=sQuery(id+"F0.wireOp",EDGE,"E28.trimOffspring");var subQ1=sQuery(id+"F0.wireOp",EDGE,"E24.trimOffspring");var subQ2=makeQuery(id+"F0.imprint","INTERSECT",VERTEX,{"derivedFrom":[subQ1,subQ0]});Q59=makeQuery(id+"F0.imprint","IMPRINT",FACE,{"disambiguationData":[TD([[makeQuery(id+"F0.imprint","IMPRINT",EDGE,{"disambiguationData":[TD([[subQ2,-1.0]])],"derivedFrom":subQ1}),1.0]])]});}
            var Q60;
            {var subQ0=sQuery(id+"F0.wireOp",EDGE,"E26.trimOffspring");var subQ1=sQuery(id+"F0.wireOp",EDGE,"E24.trimOffspring");var subQ2=makeQuery(id+"F0.imprint","INTERSECT",VERTEX,{"derivedFrom":[subQ1,subQ0]});Q60=makeQuery(id+"F0.imprint","IMPRINT",FACE,{"disambiguationData":[TD([[makeQuery(id+"F0.imprint","IMPRINT",EDGE,{"disambiguationData":[TD([[subQ2,-1.0]])],"derivedFrom":subQ1}),1.0]])]});}
            var Q61;
            {var subQ0=sQuery(id+"F0.wireOp",EDGE,"E28.trimOffspring");var subQ1=sQuery(id+"F0.wireOp",EDGE,"E26.trimOffspring");var subQ2=makeQuery(id+"F0.imprint","INTERSECT",VERTEX,{"derivedFrom":[subQ1,subQ0]});Q61=makeQuery(id+"F0.imprint","IMPRINT",FACE,{"disambiguationData":[TD([[makeQuery(id+"F0.imprint","IMPRINT",EDGE,{"disambiguationData":[TD([[subQ2,-1.0]])],"derivedFrom":subQ1}),1.0]])]});}
            var Q62;
            {var subQ0=sQuery(id+"F0.wireOp",EDGE,"E28.trimOffspring");var subQ1=sQuery(id+"F0.wireOp",EDGE,"E2");var subQ2=makeQuery(id+"F0.imprint","INTERSECT",VERTEX,{"derivedFrom":[subQ1,subQ0]});Q62=makeQuery(id+"F0.imprint","IMPRINT",FACE,{"disambiguationData":[TD([[makeQuery(id+"F0.imprint","IMPRINT",EDGE,{"disambiguationData":[TD([[subQ2,-1.0]])],"derivedFrom":subQ1}),1.0]])]});}
            var Q63;
            {var subQ0=sQuery(id+"F0.wireOp",EDGE,"E26.trimOffspring");var subQ1=sQuery(id+"F0.wireOp",EDGE,"E2");var subQ2=makeQuery(id+"F0.imprint","INTERSECT",VERTEX,{"derivedFrom":[subQ1,subQ0]});Q63=makeQuery(id+"F0.imprint","IMPRINT",FACE,{"disambiguationData":[TD([[makeQuery(id+"F0.imprint","IMPRINT",EDGE,{"disambiguationData":[TD([[subQ2,-1.0]])],"derivedFrom":subQ1}),1.0]])]});}
            var Q64;
            {var subQ0=sQuery(id+"F0.wireOp",EDGE,"E24.trimOffspring");var subQ1=sQuery(id+"F0.wireOp",EDGE,"E2");var subQ2=makeQuery(id+"F0.imprint","INTERSECT",VERTEX,{"derivedFrom":[subQ1,subQ0]});Q64=makeQuery(id+"F0.imprint","IMPRINT",FACE,{"disambiguationData":[TD([[makeQuery(id+"F0.imprint","IMPRINT",EDGE,{"disambiguationData":[TD([[subQ2,-1.0]])],"derivedFrom":subQ1}),1.0]])]});}
            var Q65;
            {var subQ0=sQuery(id+"F0.wireOp",EDGE,"E22.trimOffspring");var subQ1=sQuery(id+"F0.wireOp",EDGE,"E2");var subQ2=makeQuery(id+"F0.imprint","INTERSECT",VERTEX,{"derivedFrom":[subQ1,subQ0]});Q65=makeQuery(id+"F0.imprint","IMPRINT",FACE,{"disambiguationData":[TD([[makeQuery(id+"F0.imprint","IMPRINT",EDGE,{"disambiguationData":[TD([[subQ2,-1.0]])],"derivedFrom":subQ1}),1.0]])]});}
            extrude(context, id + "F1", {"entities" : qUnion([Q0, Q1, Q2, Q3, Q4, Q5, Q6, Q7, Q8, Q9, Q10, Q11, Q12, Q13, Q14, Q15, Q16, Q17, Q18, Q19, Q20, Q21, Q22, Q23, Q24, Q25, Q26, Q27, Q28, Q29, Q30, Q31, Q32, Q33, Q34, Q35, Q36, Q37, Q38, Q39, Q40, Q41, Q42, Q43, Q44, Q45, Q46, Q47, Q48, Q49, Q50, Q51, Q52, Q53, Q54, Q55, Q56, Q57, Q58, Q59, Q60, Q61, Q62, Q63, Q64, Q65]), "depth" : 3 * mm, "offsetDistance" : 25 * mm});
        }
    });
